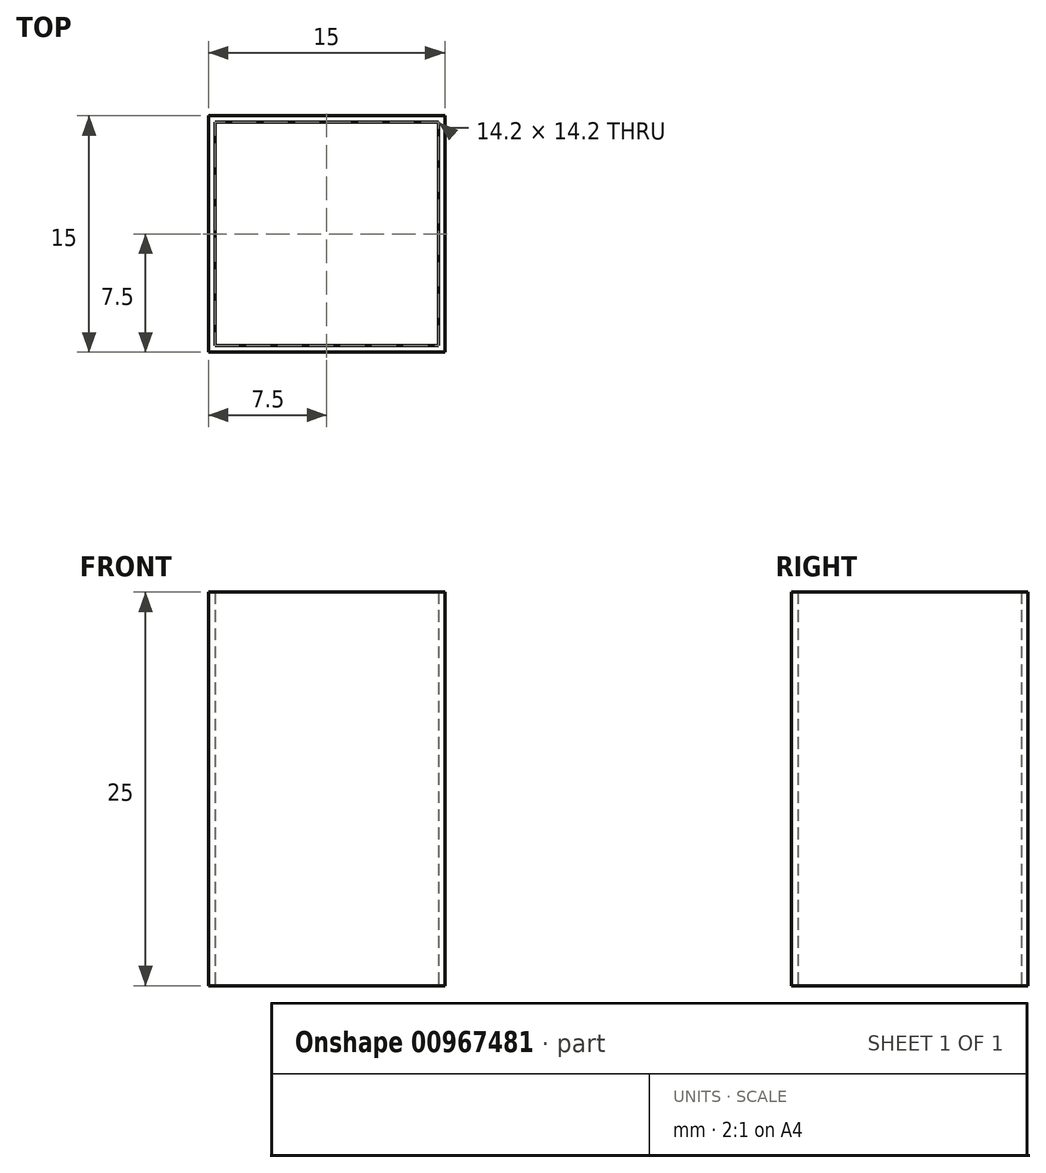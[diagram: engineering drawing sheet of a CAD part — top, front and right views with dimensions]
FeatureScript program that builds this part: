
annotation { "Feature Type Name" : "Feature", "Feature Type Description" : "" }
export const myFeature = defineFeature(function(context is Context, id is Id, definition is map)
    precondition{}
    {
        {
            var Q0;
            Q0=qCreatedBy(makeId("Top.planeOp"),FACE);
            var sketch = newSketch(context, id + "F0", { "sketchPlane" : qUnion([Q0])});
            skLineSegment(sketch, "E0.bottom", {"start": v(0, 0) * mm, "end": v(-15, 0) * mm});
            skLineSegment(sketch, "E0.top", {"start": v(0, 15) * mm, "end": v(-15, 15) * mm});
            skLineSegment(sketch, "E0.left", {"start": v(0, 0) * mm, "end": v(0, 15) * mm});
            skLineSegment(sketch, "E0.right", {"start": v(-15, 0) * mm, "end": v(-15, 15) * mm});
            skLineSegment(sketch, "E1.bottom", {"start": v(-14.6, 14.6) * mm, "end": v(-0.4, 14.6) * mm});
            skLineSegment(sketch, "E1.top", {"start": v(-14.6, 0.4) * mm, "end": v(-0.4, 0.4) * mm});
            skLineSegment(sketch, "E1.left", {"start": v(-14.6, 14.6) * mm, "end": v(-14.6, 0.4) * mm});
            skLineSegment(sketch, "E1.right", {"start": v(-0.4, 14.6) * mm, "end": v(-0.4, 0.4) * mm});
            skSolve(sketch);
        }
        {
            var Q0;
            Q0 = qSketchRegion(id + "F0", true);
            extrude(context, id + "F1", {"entities" : qUnion([Q0]), "depth" : 25 * mm, "offsetDistance" : 25 * mm});
        }
    });
